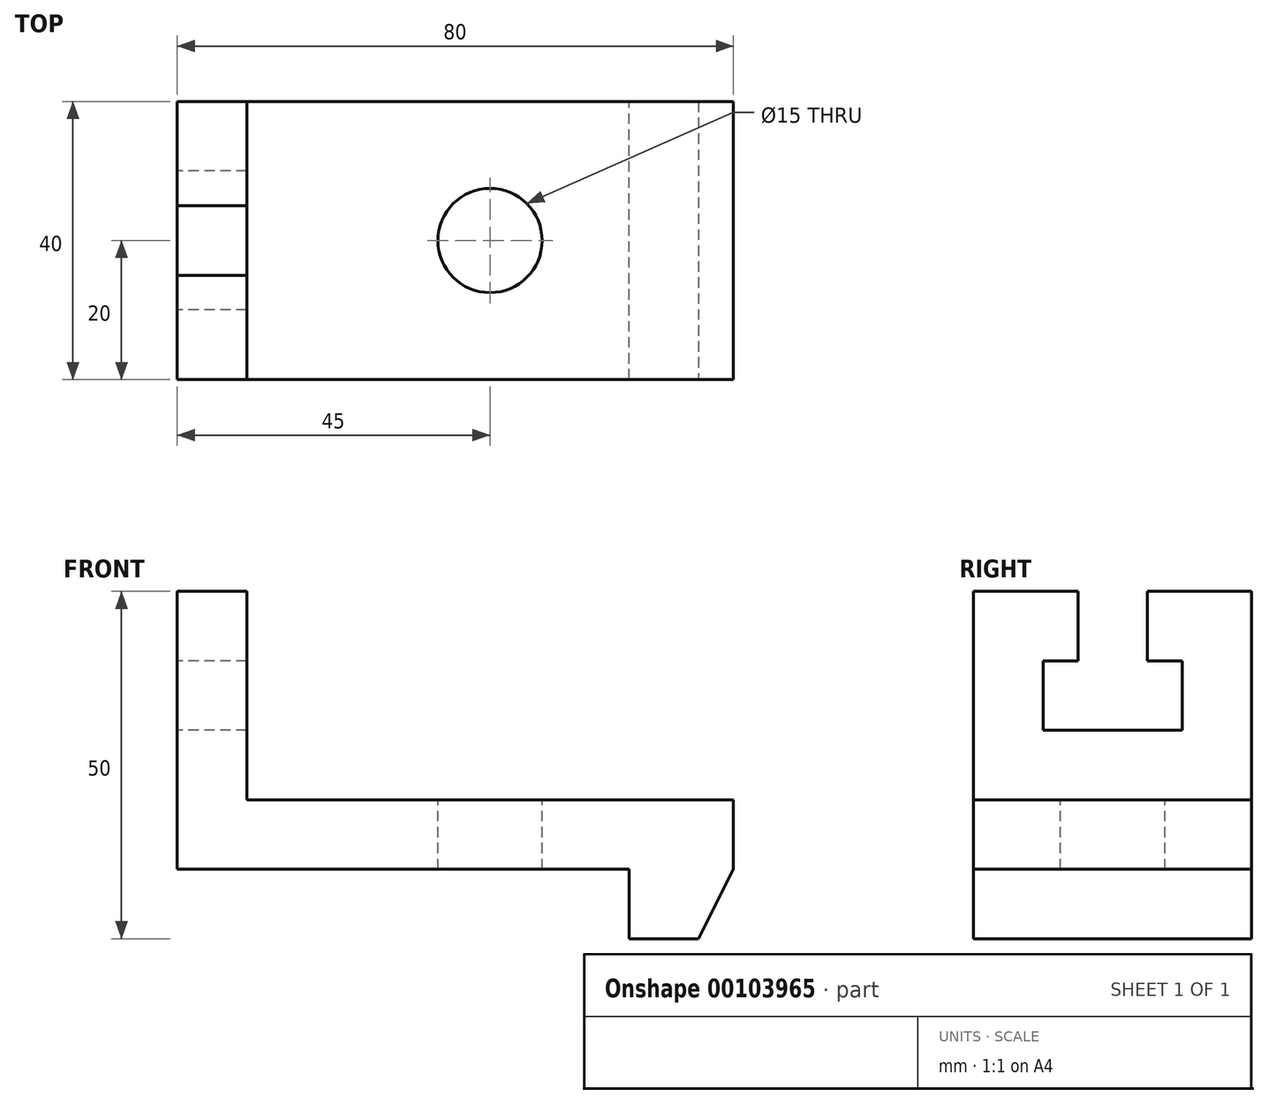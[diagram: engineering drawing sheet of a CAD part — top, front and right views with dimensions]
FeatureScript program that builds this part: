
annotation { "Feature Type Name" : "Feature", "Feature Type Description" : "" }
export const myFeature = defineFeature(function(context is Context, id is Id, definition is map)
    precondition{}
    {
        {
            var Q0;
            Q0=qCreatedBy(makeId("Top.planeOp"),FACE);
            var sketch = newSketch(context, id + "F0", { "sketchPlane" : qUnion([Q0])});
            skLineSegment(sketch, "E0.bottom", {"start": v(40, -20) * mm, "end": v(-40, -20) * mm});
            skLineSegment(sketch, "E0.top", {"start": v(40, 20) * mm, "end": v(-40, 20) * mm});
            skLineSegment(sketch, "E0.left", {"start": v(40, -20) * mm, "end": v(40, 20) * mm});
            skLineSegment(sketch, "E0.right", {"start": v(-40, -20) * mm, "end": v(-40, 20) * mm});
            skPoint(sketch, "E0.middle", {"position": v(0, 0) * mm});
            skSolve(sketch);
        }
        {
            var Q0;
            Q0 = qSketchRegion(id + "F0", true);
            extrude(context, id + "F1", {"entities" : qUnion([Q0]), "depth" : 10 * mm});
        }
        {
            var Q0;
            Q0=makeQuery(id+"F1.opExtrude","CAP_FACE",FACE,{"disambiguationData":[OSD([sQuery(id+"F0.wireOp",EDGE,"E0.bottom"),sQuery(id+"F0.wireOp",EDGE,"E0.top"),sQuery(id+"F0.wireOp",EDGE,"E0.left"),sQuery(id+"F0.wireOp",EDGE,"E0.right")])],"isStart":false});
            var sketch = newSketch(context, id + "F2", { "sketchPlane" : qUnion([Q0])});
            skLineSegment(sketch, "E1", {"start": v(-30, 20) * mm, "end": v(-30, -20) * mm});
            skSolve(sketch);
        }
        {
            var Q0;
            Q0 = qSketchRegion(id + "F2", true);
            var Q1;
            {var subQ0=sQuery(id+"F2.wireOp",EDGE,"E1");Q1=makeQuery(id+"F2.imprint","IMPRINT",FACE,{"disambiguationData":[TD([[makeQuery(id+"F2.imprint","IMPRINT",EDGE,{"derivedFrom":subQ0}),-1.0]])]});}
            extrude(context, id + "F3", {"entities" : qUnion([Q0, Q1]), "operationType" : NewBodyOperationType.ADD, "depth" : 30 * mm});
        }
        {
            var Q0;
            Q0=makeQuery(id+"F1.opExtrude","CAP_FACE",FACE,{"disambiguationData":[OSD([sQuery(id+"F0.wireOp",EDGE,"E0.bottom"),sQuery(id+"F0.wireOp",EDGE,"E0.top"),sQuery(id+"F0.wireOp",EDGE,"E0.left"),sQuery(id+"F0.wireOp",EDGE,"E0.right")])],"isStart":true});
            var sketch = newSketch(context, id + "F4", { "sketchPlane" : qUnion([Q0])});
            skLineSegment(sketch, "E2", {"start": v(25, 20) * mm, "end": v(25, -20) * mm});
            skSolve(sketch);
        }
        {
            var Q0;
            Q0 = qSketchRegion(id + "F4", true);
            var Q1;
            {var subQ0=sQuery(id+"F4.wireOp",EDGE,"E2");Q1=makeQuery(id+"F4.imprint","IMPRINT",FACE,{"disambiguationData":[TD([[makeQuery(id+"F4.imprint","IMPRINT",EDGE,{"derivedFrom":subQ0}),1.0]])]});}
            extrude(context, id + "F5", {"entities" : qUnion([Q0, Q1]), "operationType" : NewBodyOperationType.ADD, "depth" : 10 * mm});
        }
        {
            var Q0;
            {var subQ0=sQuery(id+"F0.wireOp",EDGE,"E0.bottom");Q0=makeQuery(id+"F5.boolean.opBoolean","MERGE",FACE,{"derivedFrom":[makeQuery(id+"F3.boolean.opBoolean","MERGE",FACE,{"derivedFrom":[makeQuery(id+"F1.opExtrude","SWEPT_FACE",FACE,{"disambiguationData":[OSD([subQ0])]}),makeQuery(id+"F3.opExtrude","SWEPT_FACE",FACE,{"disambiguationData":[OSD([subQ0])]})]}),makeQuery(id+"F5.opExtrude","SWEPT_FACE",FACE,{"disambiguationData":[OSD([subQ0])]})]});}
            var sketch = newSketch(context, id + "F6", { "sketchPlane" : qUnion([Q0])});
            skPoint(sketch, "E3.endSnap0", {"position": v(32.5, -10) * mm});
            skLineSegment(sketch, "E4", {"start": v(35, -10) * mm, "end": v(40, 0) * mm});
            skSolve(sketch);
        }
        {
            var Q0;
            Q0 = qSketchRegion(id + "F6", true);
            var Q1;
            {var subQ0=sQuery(id+"F6.wireOp",EDGE,"E4");Q1=makeQuery(id+"F6.imprint","IMPRINT",FACE,{"disambiguationData":[TD([[makeQuery(id+"F6.imprint","IMPRINT",EDGE,{"derivedFrom":subQ0}),-1.0]])]});}
            extrude(context, id + "F7", {"entities" : qUnion([Q0, Q1]), "operationType" : NewBodyOperationType.REMOVE, "endBound" : BoundingType.THROUGH_ALL, "oppositeDirection" : true, "depth" : 25 * mm});
        }
        {
            var Q0;
            {var subQ0=sQuery(id+"F0.wireOp",EDGE,"E0.right");Q0=makeQuery(id+"F3.boolean.opBoolean","MERGE",FACE,{"derivedFrom":[makeQuery(id+"F1.opExtrude","SWEPT_FACE",FACE,{"disambiguationData":[OSD([subQ0])]}),makeQuery(id+"F3.opExtrude","SWEPT_FACE",FACE,{"disambiguationData":[OSD([subQ0])]})]});}
            var sketch = newSketch(context, id + "F8", { "sketchPlane" : qUnion([Q0])});
            skLineSegment(sketch, "E5", {"start": v(0, 40) * mm, "end": v(0, 7.5) * mm, "construction": true});
            skPoint(sketch, "E5.endSnap0", {"position": v(0, 40) * mm});
            skLineSegment(sketch, "E6", {"start": v(-5, 40) * mm, "end": v(-5, 30) * mm});
            skLineSegment(sketch, "E7", {"start": v(5, 40) * mm, "end": v(5, 30) * mm});
            skLineSegment(sketch, "E8", {"start": v(-10, 30) * mm, "end": v(-5, 30) * mm});
            skLineSegment(sketch, "E9", {"start": v(-10, 20) * mm, "end": v(10, 20) * mm});
            skLineSegment(sketch, "E10", {"start": v(-10, 30) * mm, "end": v(-10, 20) * mm});
            skLineSegment(sketch, "E11", {"start": v(10, 40) * mm, "end": v(10, 20) * mm});
            skLineSegment(sketch, "E12.trimOffspring", {"start": v(5, 30) * mm, "end": v(10, 30) * mm});
            skSolve(sketch);
        }
        {
            var Q0;
            Q0 = qSketchRegion(id + "F8", true);
            var Q1;
            {var subQ1=sQuery(id+"F8.wireOp",EDGE,"E6");Q1=makeQuery(id+"F8.imprint","IMPRINT",FACE,{"disambiguationData":[TD([[makeQuery(id+"F8.imprint","IMPRINT",EDGE,{"derivedFrom":subQ1}),1.0]])]});}
            extrude(context, id + "F9", {"entities" : qUnion([Q0, Q1]), "operationType" : NewBodyOperationType.REMOVE, "endBound" : BoundingType.THROUGH_ALL, "oppositeDirection" : true, "depth" : 25 * mm});
        }
        {
            var Q0;
            Q0=makeQuery(id+"F1.opExtrude","CAP_FACE",FACE,{"disambiguationData":[OSD([sQuery(id+"F0.wireOp",EDGE,"E0.bottom"),sQuery(id+"F0.wireOp",EDGE,"E0.top"),sQuery(id+"F0.wireOp",EDGE,"E0.left"),sQuery(id+"F0.wireOp",EDGE,"E0.right")])],"isStart":false});
            var sketch = newSketch(context, id + "F10", { "sketchPlane" : qUnion([Q0])});
            skLineSegment(sketch, "E13", {"start": v(5, 20) * mm, "end": v(5, -20) * mm, "construction": true});
            skLineSegment(sketch, "E14", {"start": v(40, 0) * mm, "end": v(-14.71, 0) * mm, "construction": true});
            skCircle(sketch, "E15", {"center": v(5, 0) * mm, "radius": 7.5 * mm});
            skSolve(sketch);
        }
        {
            var Q0;
            Q0=makeQuery(id+"F10.imprint","IMPRINT",FACE,{"disambiguationData":[TD([[makeQuery(id+"F10.imprint","IMPRINT",EDGE,{"derivedFrom":sQuery(id+"F10.wireOp",EDGE,"E15")}),1.0]])]});
            extrude(context, id + "F11", {"entities" : qUnion([Q0]), "operationType" : NewBodyOperationType.REMOVE, "endBound" : BoundingType.THROUGH_ALL, "oppositeDirection" : true, "depth" : 25 * mm});
        }
    });
